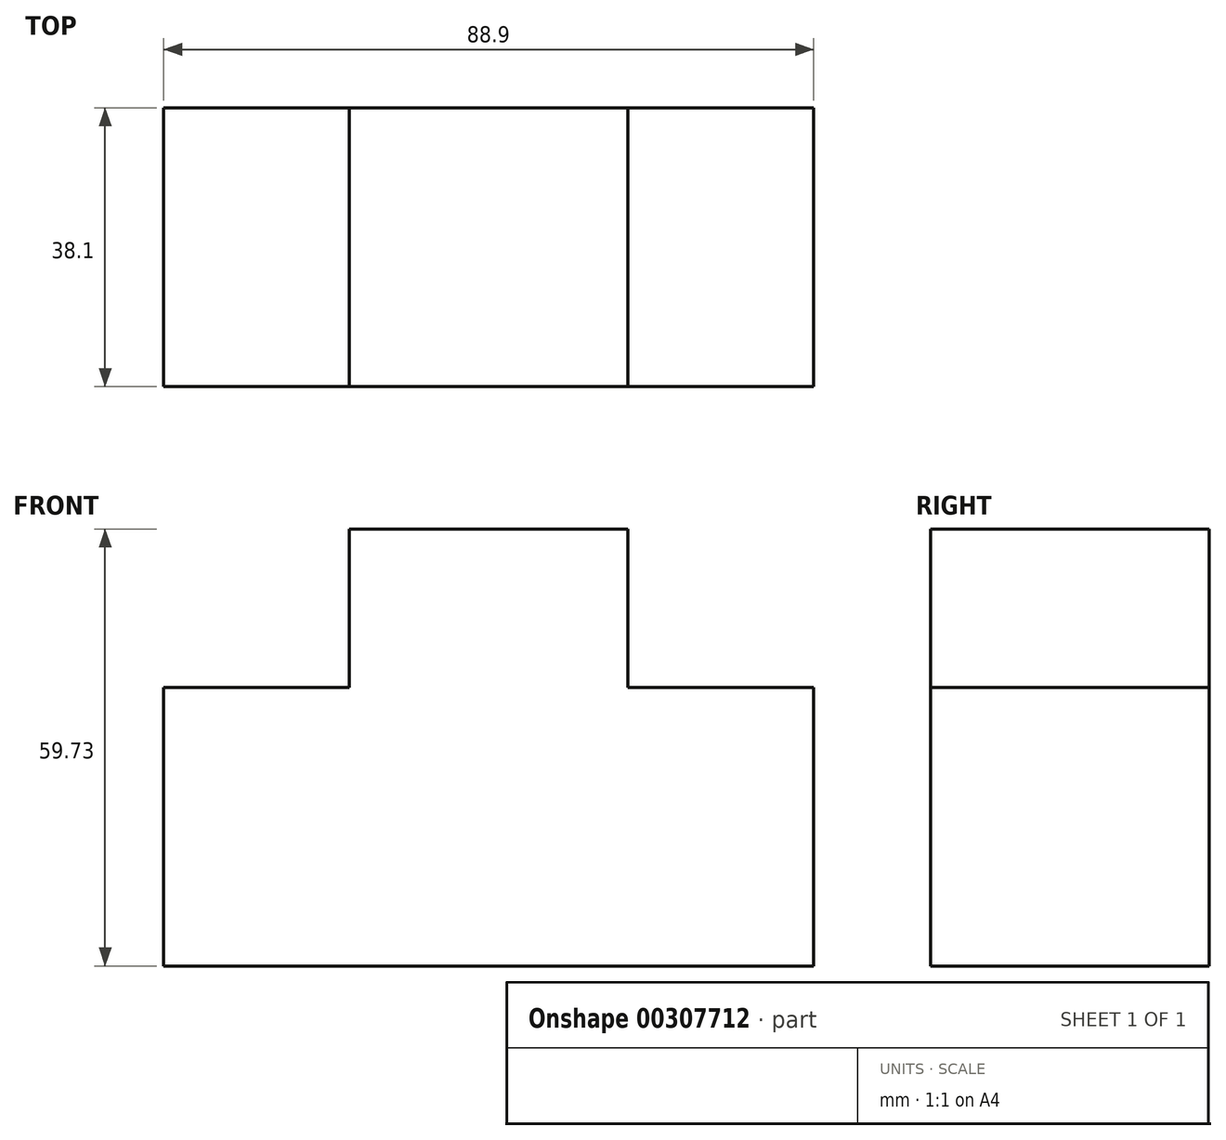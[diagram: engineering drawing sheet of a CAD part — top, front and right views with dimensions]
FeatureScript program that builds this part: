
annotation { "Feature Type Name" : "Feature", "Feature Type Description" : "" }
export const myFeature = defineFeature(function(context is Context, id is Id, definition is map)
    precondition{}
    {
        {
            var Q0;
            Q0=qCreatedBy(makeId("Front.planeOp"),FACE);
            var sketch = newSketch(context, id + "F0", { "sketchPlane" : qUnion([Q0])});
            skLineSegment(sketch, "E0", {"start": v(-46.72, -40.38) * mm, "end": v(42.18, -40.38) * mm});
            skLineSegment(sketch, "E1", {"start": v(42.18, -40.38) * mm, "end": v(42.18, -2.28) * mm});
            skLineSegment(sketch, "E2", {"start": v(42.18, -2.28) * mm, "end": v(16.78, -2.28) * mm});
            skLineSegment(sketch, "E3", {"start": v(16.78, -2.28) * mm, "end": v(16.78, 19.35) * mm});
            skLineSegment(sketch, "E4", {"start": v(16.78, 19.35) * mm, "end": v(-21.32, 19.35) * mm});
            skLineSegment(sketch, "E5", {"start": v(-21.32, 19.35) * mm, "end": v(-21.32, -2.28) * mm});
            skLineSegment(sketch, "E6", {"start": v(-21.32, -2.28) * mm, "end": v(-46.72, -2.28) * mm});
            skLineSegment(sketch, "E7", {"start": v(-46.72, -2.28) * mm, "end": v(-46.72, -40.38) * mm});
            skSolve(sketch);
        }
        {
            var Q0;
            Q0=makeQuery(id+"F0.imprint","IMPRINT",FACE,{"disambiguationData":[TD([[makeQuery(id+"F0.imprint","IMPRINT",EDGE,{"derivedFrom":sQuery(id+"F0.wireOp",EDGE,"E0")}),1.0]])]});
            extrude(context, id + "F1", {"entities" : qUnion([Q0]), "depth" : 38.1 * mm});
        }
    });
